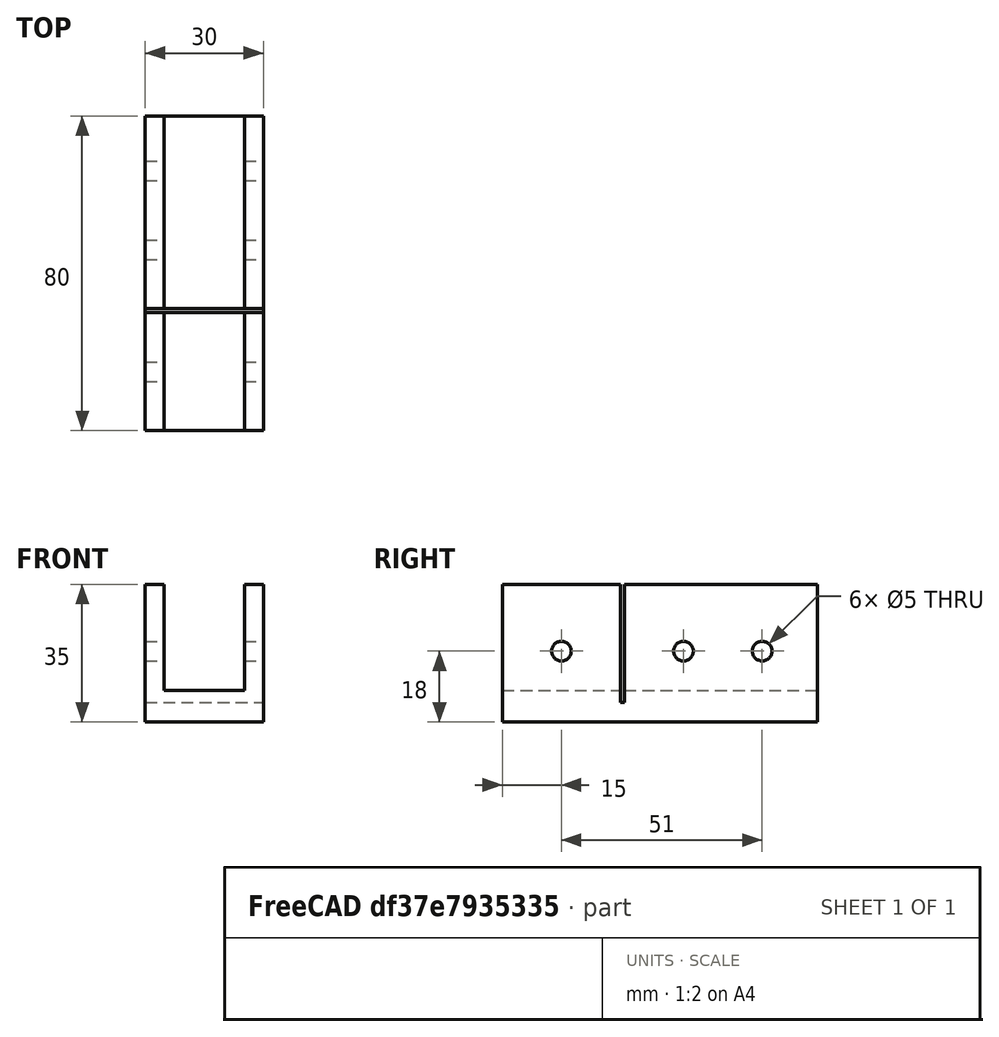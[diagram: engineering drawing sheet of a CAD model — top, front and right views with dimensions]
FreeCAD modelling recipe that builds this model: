
FCSTD DOCUMENT  (FreeCAD 0.18R)
Label: Herramienta-de-corte-2020
License: All rights reserved
LicenseURL: http://en.wikipedia.org/wiki/All_rights_reserved
objects: Part::Cut×5, Part::Box×3, Part::Cylinder×3, Part::Feature×1
note: 12 computed .brp shape members not serialized (recipe doc carries the construction recipe); baked Part::Feature solids carry a one-line shape summary decoded from their .brp

FEATURE [Part::Box] Box  label="Cubo"
  AttacherType = Attacher::AttachEngine3D
  Height = 35
  Length = 30
  Width = 80
FEATURE [Part::Box] Box001  label="Cubo001"
  AttacherType = Attacher::AttachEngine3D
  Height = 35
  Length = 20.4
  Placement = pos=(4.8,-5,8) rot=(0,0,1;0rad)
  Width = 100
FEATURE [Part::Box] Box002  label="Cubo002"
  AttacherType = Attacher::AttachEngine3D
  Height = 38
  Length = 40
  Placement = pos=(-6,30,5) rot=(0,0,1;0rad)
  Width = 1
FEATURE [Part::Cylinder] Cylinder  label="Cilindro"
  Angle = 360
  AttacherType = Attacher::AttachEngine3D
  Height = 40
  Placement = pos=(-5,15,18) rot=(0,1,0;1.5708rad)
  Radius = 2.5
FEATURE [Part::Cylinder] Cylinder001  label="Cilindro001"
  Angle = 360
  AttacherType = Attacher::AttachEngine3D
  Height = 40
  Placement = pos=(-5,46,18) rot=(0,1,0;1.5708rad)
  Radius = 2.5
FEATURE [Part::Cylinder] Cylinder002  label="Cilindro002"
  Angle = 360
  AttacherType = Attacher::AttachEngine3D
  Height = 40
  Placement = pos=(-5,66,18) rot=(0,1,0;1.5708rad)
  Radius = 2.5
FEATURE [Part::Cut] Cut
  Base = -> Box
  Tool = -> Box001
FEATURE [Part::Cut] Cut001
  Base = -> Cut
  Tool = -> Box002
FEATURE [Part::Cut] Cut002
  Base = -> Cut001
  Tool = -> Cylinder
FEATURE [Part::Cut] Cut003
  Base = -> Cut002
  Tool = -> Cylinder001
FEATURE [Part::Cut] Cut004
  Base = -> Cut003
  Tool = -> Cylinder002
FEATURE [Part::Feature] Cut004001  label="Cut005"
  shape: bbox 30 x 80 x 35 mm, 24 faces (baked)
